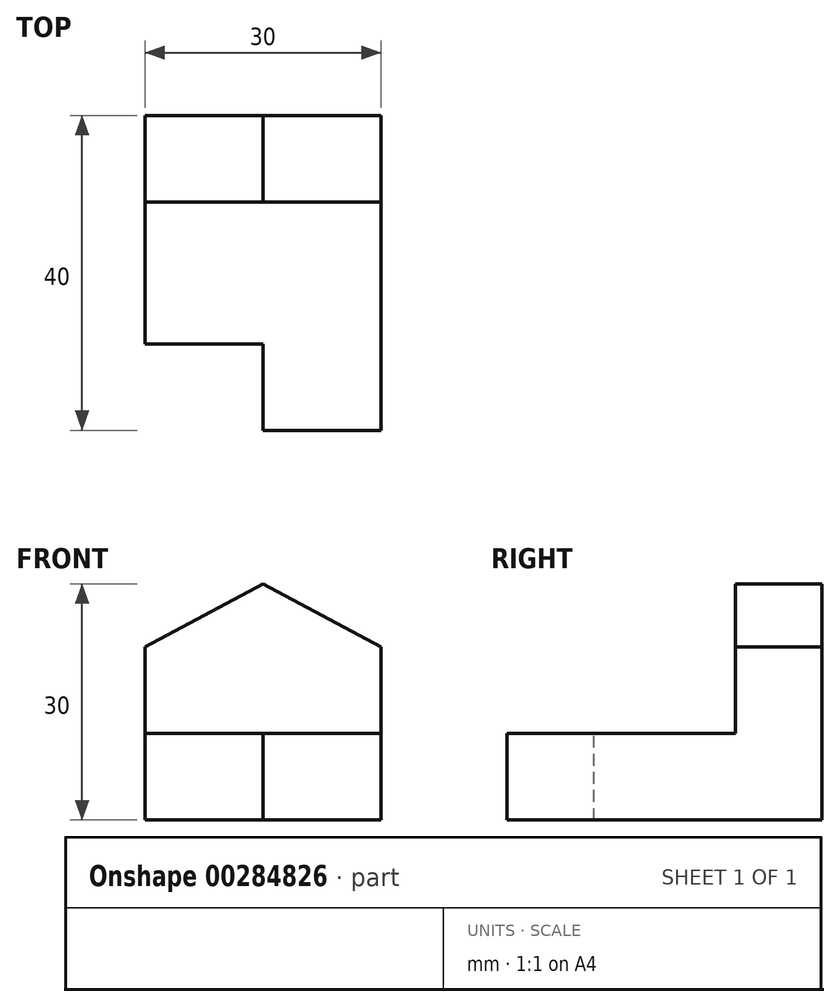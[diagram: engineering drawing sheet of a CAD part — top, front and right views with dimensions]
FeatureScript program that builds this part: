
annotation { "Feature Type Name" : "Feature", "Feature Type Description" : "" }
export const myFeature = defineFeature(function(context is Context, id is Id, definition is map)
    precondition{}
    {
        {
            var Q0;
            Q0=qCreatedBy(makeId("Front.planeOp"),FACE);
            var sketch = newSketch(context, id + "F0", { "sketchPlane" : qUnion([Q0])});
            skLineSegment(sketch, "E0.bottom", {"start": v(0, 0) * mm, "end": v(40, 0) * mm});
            skLineSegment(sketch, "E0.top", {"start": v(0, 30) * mm, "end": v(40, 30) * mm});
            skLineSegment(sketch, "E0.left", {"start": v(0, 0) * mm, "end": v(0, 30) * mm});
            skLineSegment(sketch, "E0.right", {"start": v(40, 0) * mm, "end": v(40, 30) * mm});
            skLineSegment(sketch, "E1.bottom", {"start": v(40, 30) * mm, "end": v(11, 30) * mm});
            skLineSegment(sketch, "E1.top", {"start": v(40, 11) * mm, "end": v(11, 11) * mm});
            skLineSegment(sketch, "E1.left", {"start": v(40, 30) * mm, "end": v(40, 11) * mm});
            skLineSegment(sketch, "E1.right", {"start": v(11, 30) * mm, "end": v(11, 11) * mm});
            skSolve(sketch);
        }
        {
            var Q0;
            Q0=makeQuery(id+"F0.imprint","IMPRINT",FACE,{"disambiguationData":[TD([[makeQuery(id+"F0.imprint","IMPRINT",EDGE,{"derivedFrom":sQuery(id+"F0.wireOp",EDGE,"E0.bottom")}),1.0]])]});
            extrude(context, id + "F1", {"entities" : qUnion([Q0]), "depth" : 30 * mm});
        }
        {
            var Q0;
            Q0=makeQuery(id+"F1.opExtrude","SWEPT_FACE",FACE,{"disambiguationData":[OSD([sQuery(id+"F0.wireOp",EDGE,"E1.top")])]});
            var sketch = newSketch(context, id + "F2", { "sketchPlane" : qUnion([Q0])});
            skPoint(sketch, "E2.oppositeSnap0", {"position": v(40, -15) * mm});
            skLineSegment(sketch, "E2.bottom", {"start": v(40, -30) * mm, "end": v(29, -30) * mm});
            skLineSegment(sketch, "E2.top", {"start": v(40, -15) * mm, "end": v(29, -15) * mm});
            skLineSegment(sketch, "E2.left", {"start": v(40, -30) * mm, "end": v(40, -15) * mm});
            skLineSegment(sketch, "E2.right", {"start": v(29, -30) * mm, "end": v(29, -15) * mm});
            skSolve(sketch);
        }
        {
            var Q0;
            Q0=qSketchRegion(id+"F2",true);
            var Q1;
            Q1=makeQuery(id+"F1.opExtrude","CAP_VERTEX",VERTEX,{"disambiguationData":[OSD([sQuery(id+"F0.wireOp",EDGE,"E0.bottom"),sQuery(id+"F0.wireOp",EDGE,"E0.right")])],"isStart":false});
            extrude(context, id + "F3", {"entities" : qUnion([Q0]), "operationType" : NewBodyOperationType.REMOVE, "endBound" : BoundingType.UP_TO_VERTEX, "oppositeDirection" : true, "endBoundEntityVertex" : qUnion([Q1]), "depth" : 25 * mm});
        }
        {
            var Q0;
            Q0=makeQuery(id+"F1.opExtrude","SWEPT_FACE",FACE,{"disambiguationData":[OSD([sQuery(id+"F0.wireOp",EDGE,"E1.right")])]});
            var sketch = newSketch(context, id + "F4", { "sketchPlane" : qUnion([Q0])});
            skPoint(sketch, "E3.oppositeSnap0", {"position": v(-15, 30) * mm});
            skLineSegment(sketch, "E3.bottom", {"start": v(-30, 30) * mm, "end": v(-15, 30) * mm});
            skLineSegment(sketch, "E3.top", {"start": v(-30, 22) * mm, "end": v(-15, 22) * mm});
            skLineSegment(sketch, "E3.left", {"start": v(-30, 30) * mm, "end": v(-30, 22) * mm});
            skLineSegment(sketch, "E3.right", {"start": v(-15, 30) * mm, "end": v(-15, 22) * mm});
            skSolve(sketch);
        }
        {
            var Q0;
            Q0=qSketchRegion(id+"F4",true);
            var Q1;
            Q1=makeQuery(id+"F1.opExtrude","CAP_VERTEX",VERTEX,{"disambiguationData":[OSD([sQuery(id+"F0.wireOp",EDGE,"E0.top"),sQuery(id+"F0.wireOp",EDGE,"E0.left")])],"isStart":false});
            extrude(context, id + "F5", {"entities" : qUnion([Q0]), "operationType" : NewBodyOperationType.REMOVE, "endBound" : BoundingType.UP_TO_VERTEX, "oppositeDirection" : true, "endBoundEntityVertex" : qUnion([Q1]), "depth" : 25 * mm});
        }
        {
            var Q0;
            Q0=makeQuery(id+"F1.opExtrude","SWEPT_BODY",BODY,{"disambiguationData":[OSD([sQuery(id+"F0.wireOp",EDGE,"E0.bottom"),sQuery(id+"F0.wireOp",EDGE,"E0.top"),sQuery(id+"F0.wireOp",EDGE,"E0.left"),sQuery(id+"F0.wireOp",EDGE,"E0.right"),sQuery(id+"F0.wireOp",EDGE,"E1.top"),sQuery(id+"F0.wireOp",EDGE,"E1.right")])]});
            var Q1;
            Q1=makeQuery(id+"F1.opExtrude","CAP_EDGE",EDGE,{"disambiguationData":[OSD([sQuery(id+"F0.wireOp",EDGE,"E0.left")])],"isStart":true});
            transform(context, id + "F6", {"entities" : qUnion([Q0]), "transformType" : TransformType.ROTATION, "transformAxis" : qUnion([Q1]), "angle" : 90 * degree, "oppositeDirection" : true, "makeCopy" : false});
        }
        {
            var Q0;
            Q0=makeQuery(id+"F1.opExtrude","SWEPT_FACE",FACE,{"disambiguationData":[OSD([sQuery(id+"F0.wireOp",EDGE,"E1.right")])]});
            var sketch = newSketch(context, id + "F7", { "sketchPlane" : qUnion([Q0])});
            skLineSegment(sketch, "E4", {"start": v(-15, 30) * mm, "end": v(-30, 22) * mm});
            skSolve(sketch);
        }
        {
            var Q0;
            Q0=makeQuery(id+"F7.imprint","IMPRINT",FACE,{"disambiguationData":[TD([[makeQuery(id+"F7.imprint","IMPRINT",EDGE,{"derivedFrom":sQuery(id+"F7.wireOp",EDGE,"E4")}),1.0]])]});
            var Q1;
            Q1=makeQuery(id+"F5.boolean.opBoolean","COPY",VERTEX,{"derivedFrom":makeQuery(id+"F5.opExtrude","CAP_VERTEX",VERTEX,{"disambiguationData":[OSD([sQuery(id+"F0.wireOp",EDGE,"E0.top"),sQuery(id+"F0.wireOp",EDGE,"E1.bottom"),sQuery(id+"F0.wireOp",EDGE,"E1.right"),sQuery(id+"F4.wireOp",EDGE,"E3.bottom"),sQuery(id+"F4.wireOp",EDGE,"E3.right"),dummyQuery(id+"F5.vertexPlane.planeOp",FACE)])],"isStart":false})});
            extrude(context, id + "F8", {"entities" : qUnion([Q0]), "operationType" : NewBodyOperationType.ADD, "endBound" : BoundingType.UP_TO_VERTEX, "oppositeDirection" : true, "endBoundEntityVertex" : qUnion([Q1]), "depth" : 25 * mm});
        }
        {
            var Q0;
            Q0=makeQuery(id+"F8.boolean.opBoolean","MERGE",FACE,{"derivedFrom":[makeQuery(id+"F1.opExtrude","SWEPT_FACE",FACE,{"disambiguationData":[OSD([sQuery(id+"F0.wireOp",EDGE,"E1.right")])]}),makeQuery(id+"F8.opExtrude","CAP_FACE",FACE,{"disambiguationData":[OSD([sQuery(id+"F4.wireOp",EDGE,"E3.top"),sQuery(id+"F4.wireOp",EDGE,"E3.right"),sQuery(id+"F7.wireOp",EDGE,"E4")])],"isStart":true})]});
            var sketch = newSketch(context, id + "F9", { "sketchPlane" : qUnion([Q0])});
            skLineSegment(sketch, "E5", {"start": v(-15, 30) * mm, "end": v(0, 22) * mm});
            skSolve(sketch);
        }
        {
            var Q0;
            {var subQ0=sQuery(id+"F9.wireOp",EDGE,"E5");Q0=makeQuery(id+"F9.imprint","IMPRINT",FACE,{"disambiguationData":[TD([[makeQuery(id+"F9.imprint","IMPRINT",EDGE,{"derivedFrom":subQ0}),1.0]])]});}
            var Q1;
            {var subQ0=sQuery(id+"F4.wireOp",EDGE,"E3.right");var subQ1=sQuery(id+"F0.wireOp",EDGE,"E1.right");var subQ2=sQuery(id+"F0.wireOp",EDGE,"E1.bottom");var subQ3=sQuery(id+"F0.wireOp",EDGE,"E0.top");Q1=makeQuery(id+"F8.boolean.opBoolean","MERGE",VERTEX,{"derivedFrom":[makeQuery(id+"F5.boolean.opBoolean","COPY",VERTEX,{"derivedFrom":makeQuery(id+"F5.opExtrude","CAP_VERTEX",VERTEX,{"disambiguationData":[OSD([subQ3,subQ2,subQ1,sQuery(id+"F4.wireOp",EDGE,"E3.bottom"),subQ0,dummyQuery(id+"F5.vertexPlane.planeOp",FACE)])],"isStart":false})}),makeQuery(id+"F8.opExtrude","CAP_VERTEX",VERTEX,{"disambiguationData":[OSD([subQ3,subQ2,subQ1,subQ0,sQuery(id+"F7.wireOp",EDGE,"E4"),dummyQuery(id+"F8.vertexPlane.planeOp",FACE)])],"isStart":false})]});}
            extrude(context, id + "F10", {"entities" : qUnion([Q0]), "operationType" : NewBodyOperationType.REMOVE, "endBound" : BoundingType.UP_TO_VERTEX, "oppositeDirection" : true, "endBoundEntityVertex" : qUnion([Q1]), "depth" : 25 * mm});
        }
    });
